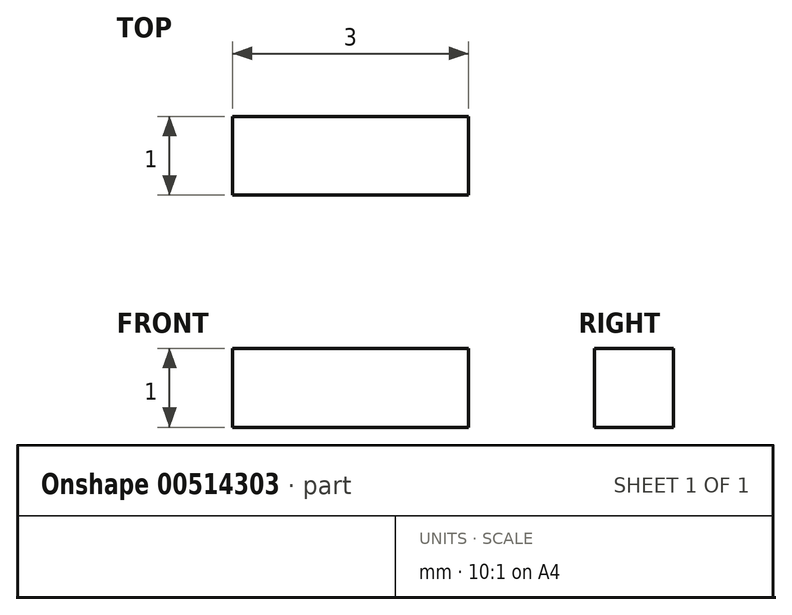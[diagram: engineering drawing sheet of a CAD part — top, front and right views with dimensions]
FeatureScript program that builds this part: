
annotation { "Feature Type Name" : "Feature", "Feature Type Description" : "" }
export const myFeature = defineFeature(function(context is Context, id is Id, definition is map)
    precondition{}
    {
        {
            var Q0;
            Q0=qCreatedBy(makeId("Top.planeOp"),FACE);
            var sketch = newSketch(context, id + "F0", { "sketchPlane" : qUnion([Q0])});
            skLineSegment(sketch, "E0.bottom", {"start": v(1.5, 0.5) * mm, "end": v(-1.5, 0.5) * mm});
            skLineSegment(sketch, "E0.top", {"start": v(1.5, -0.5) * mm, "end": v(-1.5, -0.5) * mm});
            skLineSegment(sketch, "E0.left", {"start": v(1.5, 0.5) * mm, "end": v(1.5, -0.5) * mm});
            skLineSegment(sketch, "E0.right", {"start": v(-1.5, 0.5) * mm, "end": v(-1.5, -0.5) * mm});
            skPoint(sketch, "E0.middle", {"position": v(0, 0) * mm});
            skSolve(sketch);
        }
        {
            var Q0;
            Q0 = qSketchRegion(id + "F0", true);
            extrude(context, id + "F1", {"entities" : qUnion([Q0]), "depth" : 1 * mm, "offsetDistance" : 25 * mm, "symmetric" : true});
        }
    });
